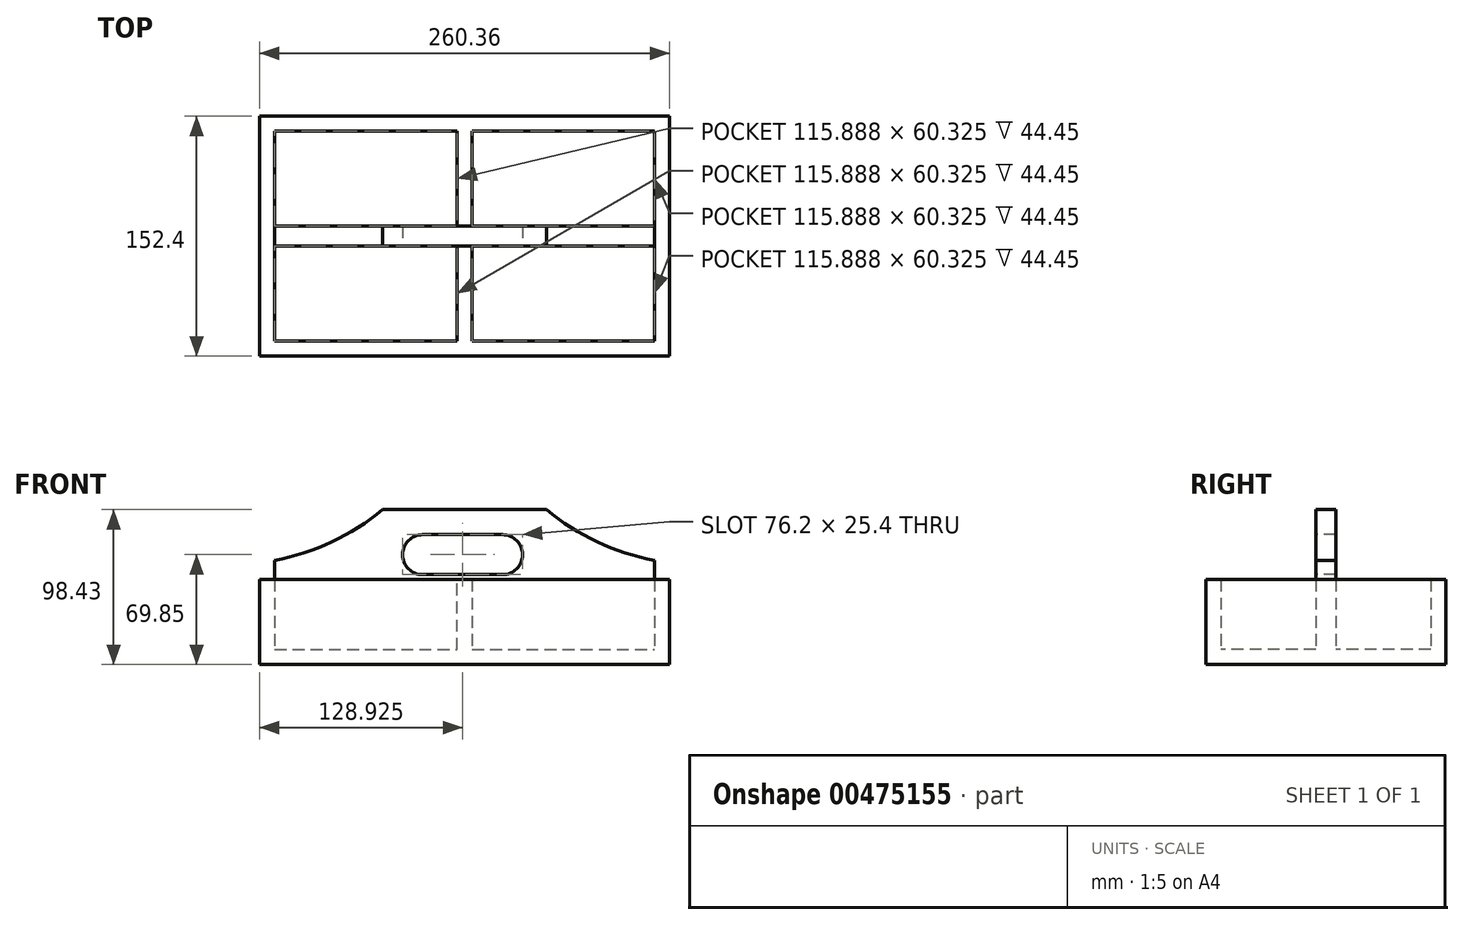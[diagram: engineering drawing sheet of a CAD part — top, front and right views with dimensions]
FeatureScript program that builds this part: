
annotation { "Feature Type Name" : "Feature", "Feature Type Description" : "" }
export const myFeature = defineFeature(function(context is Context, id is Id, definition is map)
    precondition{}
    {
        {
            var Q0;
            Q0=qCreatedBy(makeId("Front.planeOp"),FACE);
            var sketch = newSketch(context, id + "F0", { "sketchPlane" : qUnion([Q0])});
            skLineSegment(sketch, "E0", {"start": v(-130.18, 0) * mm, "end": v(130.18, 0) * mm});
            skLineSegment(sketch, "E1", {"start": v(-130.18, 0) * mm, "end": v(-130.18, 9.52) * mm});
            skLineSegment(sketch, "E2", {"start": v(130.18, 0) * mm, "end": v(130.18, 9.52) * mm});
            skLineSegment(sketch, "E3", {"start": v(-130.18, 9.53) * mm, "end": v(130.18, 9.53) * mm});
            skSolve(sketch);
        }
        {
            var Q0;
            Q0=makeQuery(id+"F0.imprint","IMPRINT",FACE,{"disambiguationData":[TD([[makeQuery(id+"F0.imprint","IMPRINT",EDGE,{"derivedFrom":sQuery(id+"F0.wireOp",EDGE,"E0")}),1.0]])]});
            extrude(context, id + "F1", {"entities" : qUnion([Q0]), "depth" : 152.4 * mm, "symmetric" : true});
        }
        {
            var Q0;
            Q0=makeQuery(id+"F1.opExtrude","SWEPT_FACE",FACE,{"disambiguationData":[OSD([sQuery(id+"F0.wireOp",EDGE,"E3")])]});
            var sketch = newSketch(context, id + "F2", { "sketchPlane" : qUnion([Q0])});
            skLineSegment(sketch, "E4", {"start": v(-130.18, 76.2) * mm, "end": v(-130.18, -76.2) * mm});
            skLineSegment(sketch, "E5", {"start": v(-130.18, -76.2) * mm, "end": v(130.18, -76.2) * mm});
            skLineSegment(sketch, "E6", {"start": v(130.18, -76.2) * mm, "end": v(130.18, 76.2) * mm});
            skLineSegment(sketch, "E7", {"start": v(130.18, 76.2) * mm, "end": v(-130.18, 76.2) * mm});
            skLineSegment(sketch, "E8", {"start": v(-120.65, 66.67) * mm, "end": v(-120.65, -66.67) * mm});
            skLineSegment(sketch, "E9", {"start": v(-120.65, -66.67) * mm, "end": v(120.65, -66.67) * mm});
            skLineSegment(sketch, "E10", {"start": v(120.65, -66.67) * mm, "end": v(120.65, 66.67) * mm});
            skLineSegment(sketch, "E11", {"start": v(-120.65, 66.67) * mm, "end": v(120.65, 66.67) * mm});
            skSolve(sketch);
        }
        {
            var Q0;
            Q0 = qSketchRegion(id + "F2", true);
            extrude(context, id + "F3", {"entities" : qUnion([Q0]), "operationType" : NewBodyOperationType.ADD, "depth" : 44.45 * mm});
        }
        {
            var Q0;
            Q0=makeQuery(id+"F1.opExtrude","SWEPT_FACE",FACE,{"disambiguationData":[OSD([sQuery(id+"F0.wireOp",EDGE,"E3")])]});
            var sketch = newSketch(context, id + "F4", { "sketchPlane" : qUnion([Q0])});
            skLineSegment(sketch, "E12", {"start": v(0, 66.67) * mm, "end": v(0, -66.67) * mm, "construction": true});
            skLineSegment(sketch, "E13", {"start": v(-120.65, 0) * mm, "end": v(120.65, 0) * mm, "construction": true});
            skLineSegment(sketch, "E14", {"start": v(0, -66.67) * mm, "end": v(4.76, -66.67) * mm});
            skLineSegment(sketch, "E15", {"start": v(4.76, -66.67) * mm, "end": v(4.76, 66.67) * mm});
            skLineSegment(sketch, "E16", {"start": v(4.76, 66.67) * mm, "end": v(0, 66.67) * mm});
            skLineSegment(sketch, "E17", {"start": v(0, 66.67) * mm, "end": v(-4.76, 66.67) * mm});
            skLineSegment(sketch, "E18", {"start": v(-4.76, 66.67) * mm, "end": v(-4.76, -66.67) * mm});
            skLineSegment(sketch, "E19", {"start": v(-4.76, -66.67) * mm, "end": v(0, -66.67) * mm});
            skSolve(sketch);
        }
        {
            var Q0;
            Q0 = qSketchRegion(id + "F4", true);
            extrude(context, id + "F5", {"entities" : qUnion([Q0]), "operationType" : NewBodyOperationType.ADD, "depth" : 44.45 * mm});
        }
        {
            var Q0;
            Q0=makeQuery(id+"F5.boolean.opBoolean","SPLIT",FACE,{"disambiguationData":[TD([makeQuery(id+"F3.opExtrude","SWEPT_FACE",FACE,{"disambiguationData":[OSD([sQuery(id+"F2.wireOp",EDGE,"E8")])]})])],"derivedFrom":makeQuery(id+"F1.opExtrude","SWEPT_FACE",FACE,{"disambiguationData":[OSD([sQuery(id+"F0.wireOp",EDGE,"E3")])]})});
            var sketch = newSketch(context, id + "F6", { "sketchPlane" : qUnion([Q0])});
            skLineSegment(sketch, "E20", {"start": v(-120.65, 0) * mm, "end": v(-120.65, 6.35) * mm});
            skLineSegment(sketch, "E21", {"start": v(-120.65, 6.35) * mm, "end": v(120.65, 6.35) * mm});
            skLineSegment(sketch, "E22", {"start": v(120.65, 6.35) * mm, "end": v(120.65, -6.35) * mm});
            skLineSegment(sketch, "E23", {"start": v(120.65, -6.35) * mm, "end": v(-120.65, -6.35) * mm});
            skLineSegment(sketch, "E24", {"start": v(-120.65, -6.35) * mm, "end": v(-120.65, 0) * mm});
            skSolve(sketch);
        }
        {
            var Q0;
            Q0 = qSketchRegion(id + "F6", true);
            extrude(context, id + "F7", {"entities" : qUnion([Q0]), "operationType" : NewBodyOperationType.ADD, "depth" : 88.9 * mm});
        }
        {
            var Q0;
            Q0=makeQuery(id+"F7.opExtrude","SWEPT_FACE",FACE,{"disambiguationData":[OSD([sQuery(id+"F6.wireOp",EDGE,"E23")])]});
            var sketch = newSketch(context, id + "F8", { "sketchPlane" : qUnion([Q0])});
            skLineSegment(sketch, "E25", {"start": v(0, 98.43) * mm, "end": v(0, 53.98) * mm, "construction": true});
            skArc(sketch, "E26", {"start": v(24.15, 82.55) * mm, "mid": v(36.85, 69.85) * mm, "end": v(24.15, 57.15) * mm});
            skArc(sketch, "E27", {"start": v(-26.65, 82.55) * mm, "mid": v(-39.35, 69.85) * mm, "end": v(-26.65, 57.15) * mm});
            skLineSegment(sketch, "E28", {"start": v(-26.65, 82.55) * mm, "end": v(24.15, 82.55) * mm});
            skLineSegment(sketch, "E29", {"start": v(24.15, 57.15) * mm, "end": v(-26.65, 57.15) * mm});
            skSolve(sketch);
        }
        {
            var Q0;
            Q0 = qSketchRegion(id + "F8", true);
            extrude(context, id + "F9", {"entities" : qUnion([Q0]), "operationType" : NewBodyOperationType.REMOVE, "oppositeDirection" : true, "depth" : 12.7 * mm});
        }
        {
            var Q0;
            Q0=makeQuery(id+"F3.boolean.opBoolean","MERGE",FACE,{"derivedFrom":[makeQuery(id+"F1.opExtrude","CAP_FACE",FACE,{"disambiguationData":[OSD([sQuery(id+"F0.wireOp",EDGE,"E0"),sQuery(id+"F0.wireOp",EDGE,"E1"),sQuery(id+"F0.wireOp",EDGE,"E2"),sQuery(id+"F0.wireOp",EDGE,"E3")])],"isStart":false}),makeQuery(id+"F3.opExtrude","SWEPT_FACE",FACE,{"disambiguationData":[OSD([sQuery(id+"F2.wireOp",EDGE,"E5")])]})]});
            var sketch = newSketch(context, id + "F10", { "sketchPlane" : qUnion([Q0])});
            skLineSegment(sketch, "E30", {"start": v(166.46, 63.5) * mm, "end": v(-215.29, 63.5) * mm});
            skLineSegment(sketch, "E31", {"start": v(-130.18, 0) * mm, "end": v(-149.14, 0) * mm});
            skLineSegment(sketch, "E32", {"start": v(-149.14, 0) * mm, "end": v(-149.14, 215.9) * mm});
            skCircle(sketch, "E33", {"center": v(-149.14, 215.9) * mm, "radius": 152.4 * mm});
            skLineSegment(sketch, "E34", {"start": v(130.18, 0) * mm, "end": v(149.14, 0) * mm});
            skLineSegment(sketch, "E35", {"start": v(149.14, 0) * mm, "end": v(149.14, 215.9) * mm});
            skCircle(sketch, "E36", {"center": v(149.14, 215.9) * mm, "radius": 152.4 * mm});
            skSolve(sketch);
        }
        {
            var Q0;
            {var subQ0=sQuery(id+"F10.wireOp",EDGE,"E33");var subQ2=sQuery(id+"F10.wireOp",EDGE,"E36");var subQ3=makeQuery(id+"F10.imprint","INTERSECT",VERTEX,{"disambiguationData":[OD(0.0)],"derivedFrom":[subQ0,subQ2]});Q0=makeQuery(id+"F10.imprint","IMPRINT",FACE,{"disambiguationData":[TD([[makeQuery(id+"F10.imprint","IMPRINT",EDGE,{"disambiguationData":[TD([[subQ3,-1.0]])],"derivedFrom":subQ2}),-1.0]])]});}
            var Q1;
            {var subQ0=sQuery(id+"F10.wireOp",EDGE,"E36");var subQ1=sQuery(id+"F10.wireOp",EDGE,"E33");var subQ2=makeQuery(id+"F10.imprint","INTERSECT",VERTEX,{"disambiguationData":[OD(0.0)],"derivedFrom":[subQ1,subQ0]});Q1=makeQuery(id+"F10.imprint","IMPRINT",FACE,{"disambiguationData":[TD([[makeQuery(id+"F10.imprint","IMPRINT",EDGE,{"disambiguationData":[TD([[subQ2,1.0]])],"derivedFrom":subQ1}),1.0]])]});}
            var Q2;
            {var subQ0=sQuery(id+"F10.wireOp",EDGE,"E36");var subQ1=sQuery(id+"F10.wireOp",EDGE,"E33");var subQ2=makeQuery(id+"F10.imprint","INTERSECT",VERTEX,{"disambiguationData":[OD(0.0)],"derivedFrom":[subQ1,subQ0]});Q2=makeQuery(id+"F10.imprint","IMPRINT",FACE,{"disambiguationData":[TD([[makeQuery(id+"F10.imprint","IMPRINT",EDGE,{"disambiguationData":[TD([[subQ2,1.0]])],"derivedFrom":subQ1}),-1.0]])]});}
            extrude(context, id + "F11", {"entities" : qUnion([Q0, Q1, Q2]), "operationType" : NewBodyOperationType.REMOVE, "oppositeDirection" : true, "depth" : 223.52 * mm});
        }
    });
